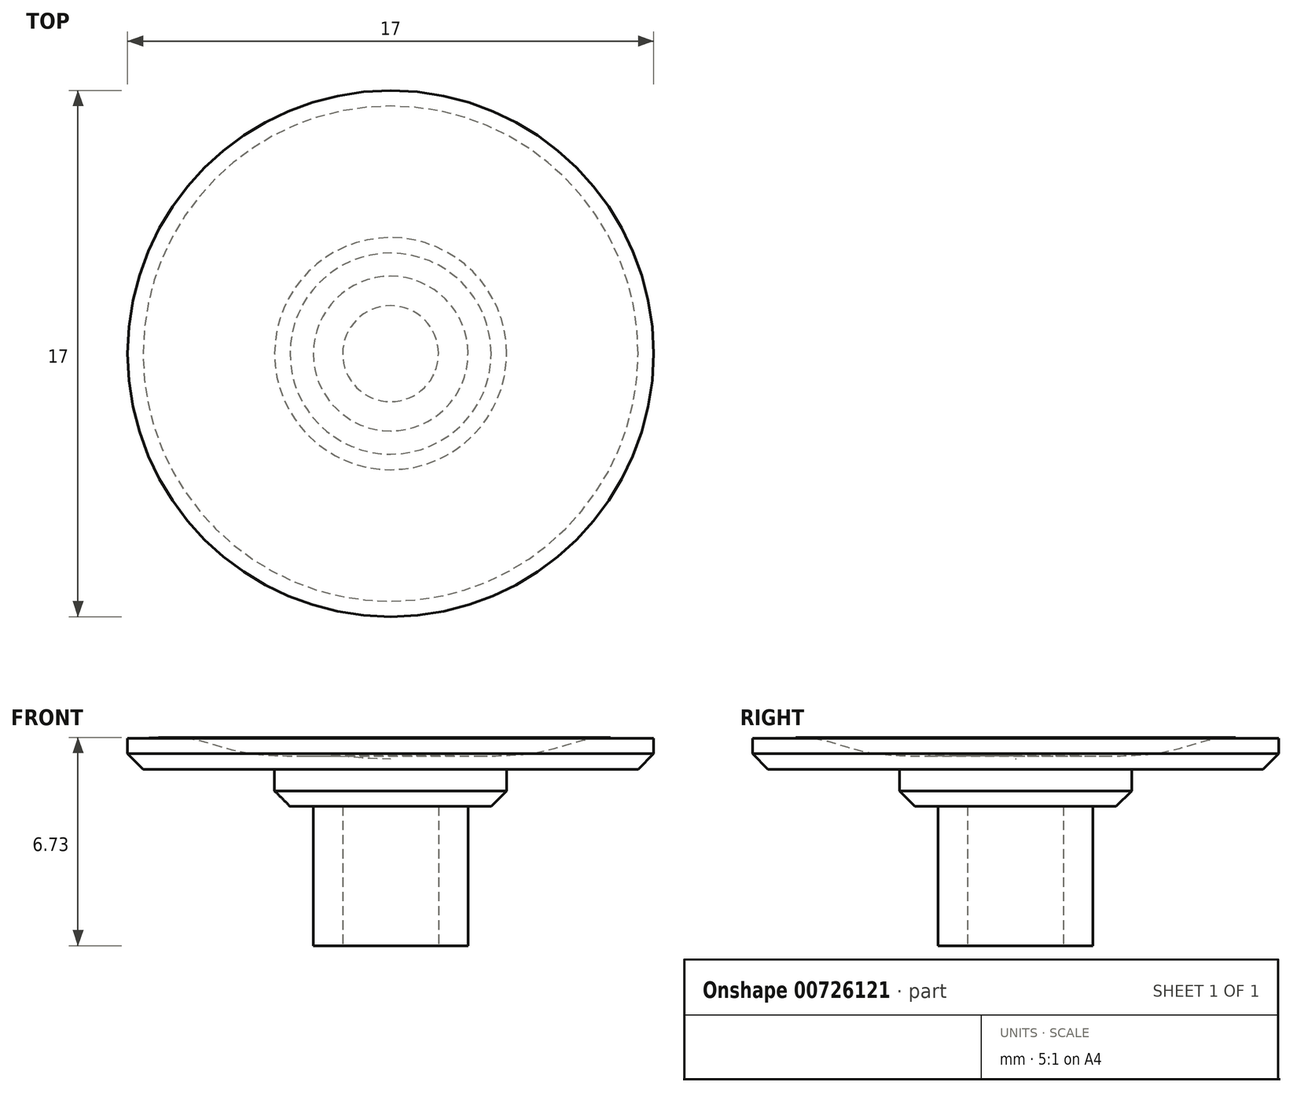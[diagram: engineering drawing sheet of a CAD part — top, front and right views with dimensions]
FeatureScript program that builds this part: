
annotation { "Feature Type Name" : "Feature", "Feature Type Description" : "" }
export const myFeature = defineFeature(function(context is Context, id is Id, definition is map)
    precondition{}
    {
        {
            var Q0;
            Q0=qCreatedBy(makeId("Front.planeOp"),FACE);
            var sketch = newSketch(context, id + "F0", { "sketchPlane" : qUnion([Q0])});
            skLineSegment(sketch, "E0", {"start": v(0, 0) * mm, "end": v(-8.5, 0) * mm});
            skLineSegment(sketch, "E1", {"start": v(-8.5, 0) * mm, "end": v(-8.5, 1) * mm});
            skFitSpline(sketch, "E2", {"points": [v(-8.5, 1) * mm, v(-6.57, 1) * mm, v(-4.65, 0.53) * mm, v(-1.66, 0.43) * mm, v(0, 0.35) * mm], "startDerivative": vector(6.97, -0.38) * mm, "endDerivative": vector(11.67, 0) * mm});
            skLineSegment(sketch, "E3", {"start": v(0, 0.35) * mm, "end": v(0, 0) * mm});
            skLineSegment(sketch, "E4", {"start": v(0, 0) * mm, "end": v(0, 1.2) * mm, "construction": true});
            skLineSegment(sketch, "E5", {"start": v(-8.5, 0) * mm, "end": v(-4.25, 0) * mm, "construction": true});
            skSolve(sketch);
        }
        {
            var Q0;
            Q0 = qSketchRegion(id + "F0", true);
            var Q1;
            Q1=sQuery(id+"F0.wireOp",EDGE,"E4");
            revolve(context, id + "F1", {"surfaceOperationType" : NewSurfaceOperationType.NEW, "entities" : qUnion([Q0]), "axis" : qUnion([Q1]), "revolveType" : RevolveType.FULL});
        }
        {
            var Q0;
            Q0=makeQuery(id+"F1.opRevolve","SWEPT_FACE",FACE,{"disambiguationData":[OSD([sQuery(id+"F0.wireOp",EDGE,"E0")])]});
            var sketch = newSketch(context, id + "F2", { "sketchPlane" : qUnion([Q0])});
            skCircle(sketch, "E6", {"center": v(0, 0) * mm, "radius": 3.75 * mm});
            skSolve(sketch);
        }
        {
            var Q0;
            Q0 = qSketchRegion(id + "F2", true);
            extrude(context, id + "F3", {"entities" : qUnion([Q0]), "operationType" : NewBodyOperationType.ADD, "depth" : 1.2 * mm, "offsetDistance" : 25 * mm});
        }
        {
            var Q0;
            Q0=makeQuery(id+"F3.opExtrude","CAP_FACE",FACE,{"disambiguationData":[OSD([sQuery(id+"F2.wireOp",EDGE,"E6")])],"isStart":false});
            var sketch = newSketch(context, id + "F4", { "sketchPlane" : qUnion([Q0])});
            skPoint(sketch, "E7", {"position": v(0, 0) * mm});
            skCircle(sketch, "E8", {"center": v(0, 0) * mm, "radius": 2.5 * mm});
            skSolve(sketch);
        }
        {
            var Q0;
            Q0=makeQuery(id+"F4.imprint","IMPRINT",FACE,{"disambiguationData":[TD([[makeQuery(id+"F4.imprint","IMPRINT",EDGE,{"derivedFrom":sQuery(id+"F4.wireOp",EDGE,"E8")}),1.0]])]});
            extrude(context, id + "F5", {"entities" : qUnion([Q0]), "operationType" : NewBodyOperationType.ADD, "depth" : 4.5 * mm, "offsetDistance" : 25 * mm});
        }
        {
            var Q0;
            Q0=makeQuery(id+"F5.opExtrude","CAP_FACE",FACE,{"disambiguationData":[OSD([sQuery(id+"F4.wireOp",EDGE,"E8")])],"isStart":false});
            var sketch = newSketch(context, id + "F6", { "sketchPlane" : qUnion([Q0])});
            skPoint(sketch, "E9", {"position": v(0, 0) * mm});
            skCircle(sketch, "E10", {"center": v(0, 0) * mm, "radius": 1.55 * mm});
            skSolve(sketch);
        }
        {
            var Q0;
            Q0 = qSketchRegion(id + "F6", true);
            var Q1;
            Q1=makeQuery(id+"F3.opExtrude","CAP_FACE",FACE,{"disambiguationData":[OSD([sQuery(id+"F2.wireOp",EDGE,"E6")])],"isStart":false});
            extrude(context, id + "F7", {"entities" : qUnion([Q0]), "operationType" : NewBodyOperationType.REMOVE, "endBound" : BoundingType.UP_TO_SURFACE, "oppositeDirection" : true, "depth" : 3.5 * mm, "endBoundEntityFace" : qUnion([Q1]), "offsetDistance" : 25 * mm});
        }
        {
            var Q0;
            Q0=makeQuery(id+"F3.opExtrude","CAP_EDGE",EDGE,{"disambiguationData":[OSD([sQuery(id+"F2.wireOp",EDGE,"E6")])],"isStart":false});
            var Q1;
            Q1=makeQuery(id+"F1.opRevolve","SWEPT_EDGE",EDGE,{"disambiguationData":[OSD([sQuery(id+"F0.wireOp",EDGE,"E0"),sQuery(id+"F0.wireOp",EDGE,"E1")])]});
            chamfer(context, id + "F8", {"entities" : qUnion([Q0, Q1]), "chamferType" : ChamferType.OFFSET_ANGLE, "width" : .5 * mm, "oppositeDirection" : false, "angle" : 45 * degree, "tangentPropagation" : true});
        }
    });
